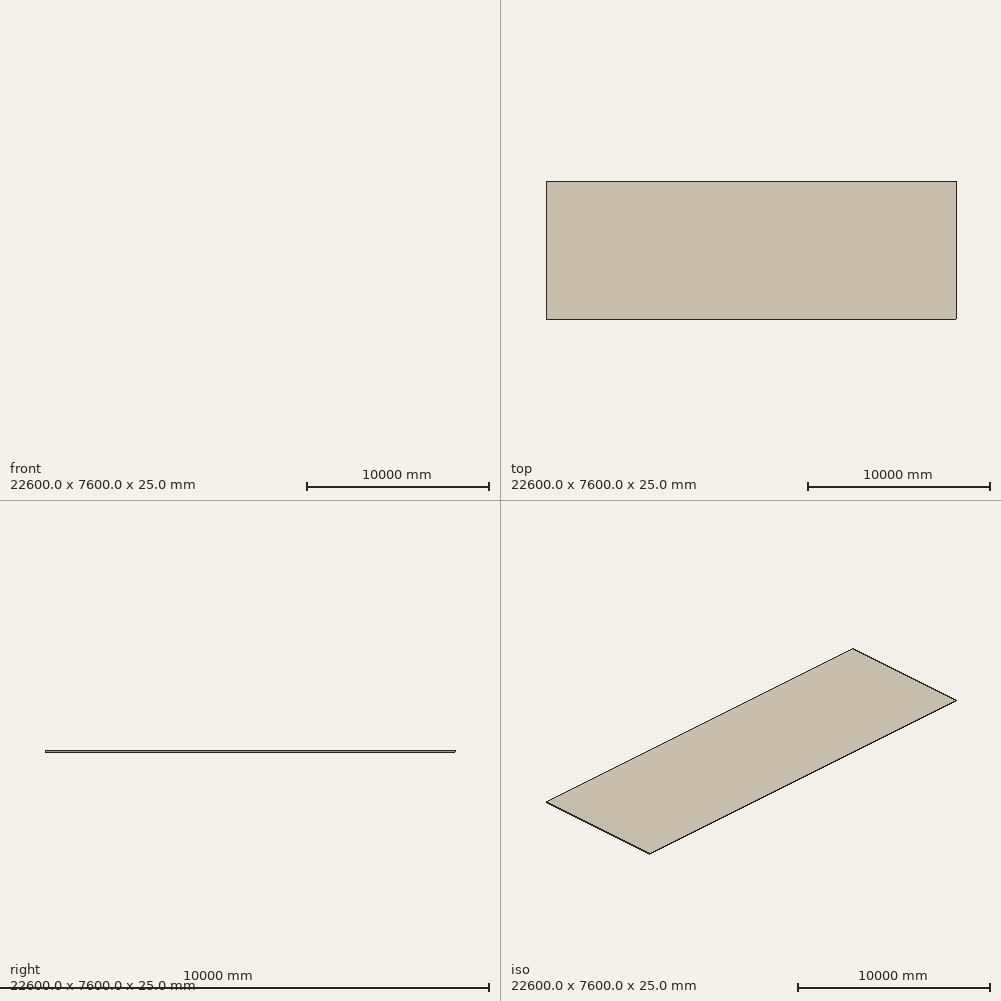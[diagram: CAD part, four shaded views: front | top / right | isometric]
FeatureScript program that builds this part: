
annotation { "Feature Type Name" : "Feature", "Feature Type Description" : "" }
export const myFeature = defineFeature(function(context is Context, id is Id, definition is map)
    precondition{}
    {
        {
            var Q0;
            Q0=qCreatedBy(makeId("Top.planeOp"),FACE);
            var sketch = newSketch(context, id + "F0", { "sketchPlane" : qUnion([Q0])});
            skLineSegment(sketch, "E0.bottom", {"start": v(0, 0) * mm, "end": v(22600, 0) * mm});
            skLineSegment(sketch, "E0.top", {"start": v(0, 7600) * mm, "end": v(22600, 7600) * mm});
            skLineSegment(sketch, "E0.left", {"start": v(0, 0) * mm, "end": v(0, 7600) * mm});
            skLineSegment(sketch, "E0.right", {"start": v(22600, 0) * mm, "end": v(22600, 7600) * mm});
            skSolve(sketch);
        }
        {
            var Q0;
            Q0 = qSketchRegion(id + "F0", true);
            extrude(context, id + "F1", {"entities" : qUnion([Q0]), "depth" : 25 * mm, "offsetDistance" : 25 * mm});
        }
    });
